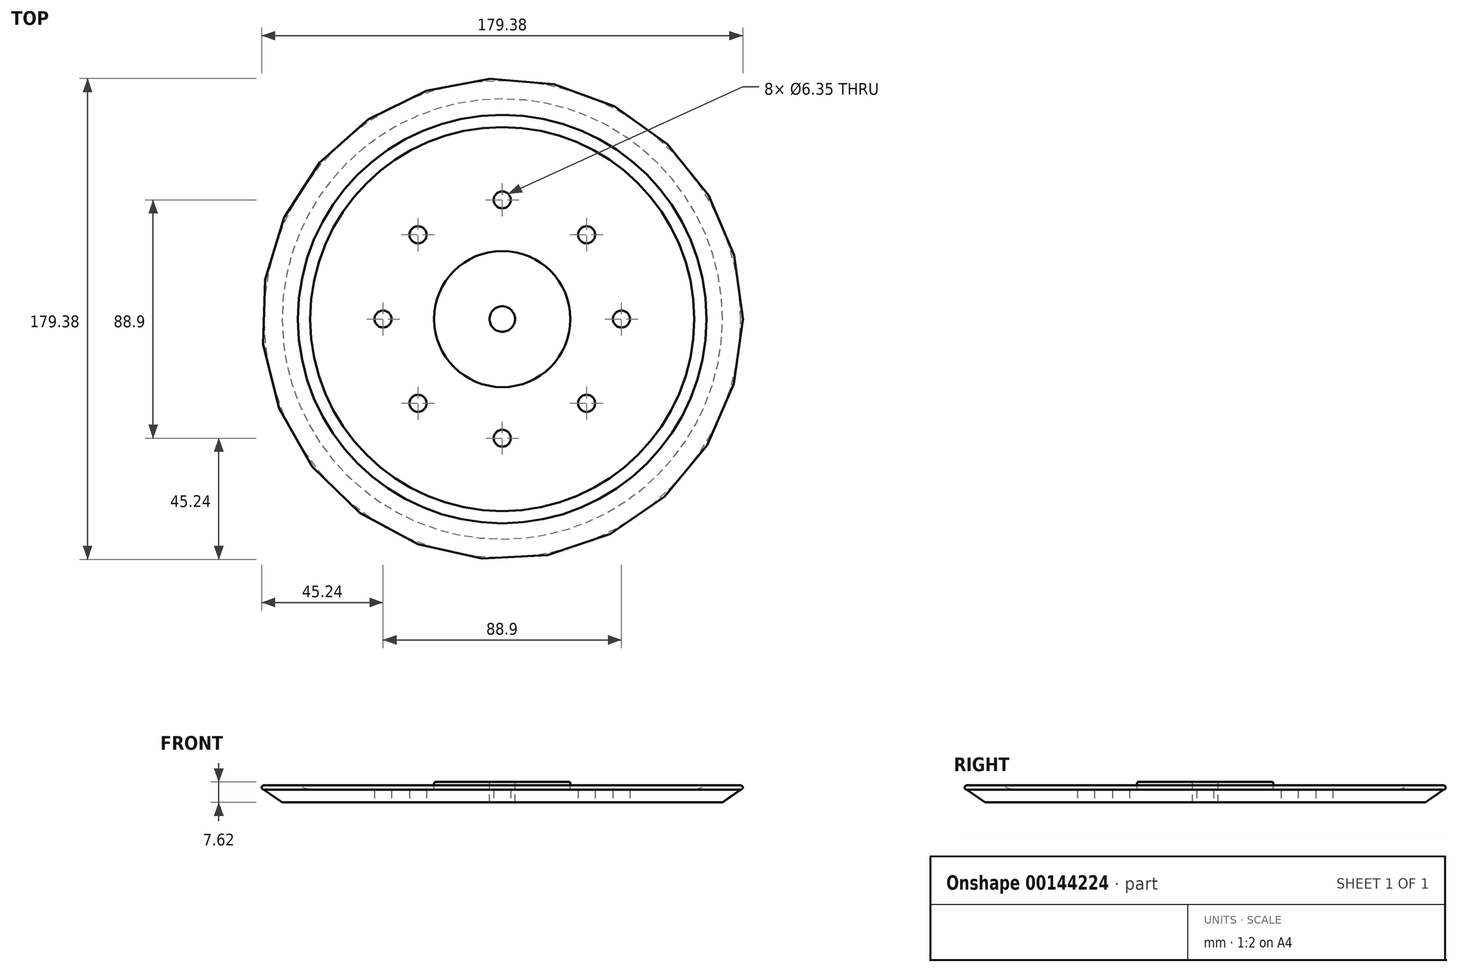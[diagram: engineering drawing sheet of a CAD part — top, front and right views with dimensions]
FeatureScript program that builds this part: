
annotation { "Feature Type Name" : "Feature", "Feature Type Description" : "" }
export const myFeature = defineFeature(function(context is Context, id is Id, definition is map)
    precondition{}
    {
        {
            var Q0;
            Q0=qCreatedBy(makeId("Front.planeOp"),FACE);
            var sketch = newSketch(context, id + "F0", { "sketchPlane" : qUnion([Q0])});
            skLineSegment(sketch, "E0", {"start": v(0, 0) * mm, "end": v(0, 7.62) * mm});
            skLineSegment(sketch, "E1", {"start": v(88.9, 4.76) * mm, "end": v(82.1, 0) * mm});
            skLineSegment(sketch, "E2", {"start": v(82.1, 0) * mm, "end": v(0, 0) * mm});
            skLineSegment(sketch, "E3", {"start": v(88.9, 6.35) * mm, "end": v(76.2, 6.35) * mm});
            skLineSegment(sketch, "E4", {"start": v(76.2, 6.35) * mm, "end": v(71.63, 4.57) * mm});
            skLineSegment(sketch, "E5", {"start": v(71.63, 4.57) * mm, "end": v(25.4, 4.57) * mm});
            skLineSegment(sketch, "E6", {"start": v(25.4, 4.57) * mm, "end": v(25.4, 7.1) * mm});
            skLineSegment(sketch, "E7", {"start": v(24.89, 7.62) * mm, "end": v(0, 7.62) * mm});
            skArc(sketch, "E8", {"start": v(88.9, 4.76) * mm, "mid": v(89.7, 5.56) * mm, "end": v(88.9, 6.35) * mm});
            skLineSegment(sketch, "E9.bottom", {"start": v(0, 7.62) * mm, "end": v(4.76, 7.62) * mm});
            skLineSegment(sketch, "E9.top", {"start": v(0, 0) * mm, "end": v(4.76, 0) * mm});
            skLineSegment(sketch, "E9.left", {"start": v(0, 7.62) * mm, "end": v(0, 0) * mm});
            skLineSegment(sketch, "E9.right", {"start": v(4.76, 7.62) * mm, "end": v(4.76, 0) * mm});
            skPoint(sketch, "E10.visualSharp", {"position": v(25.4, 7.62) * mm});
            skArc(sketch, "E10.filletArc", {"start": v(25.4, 7.1) * mm, "mid": v(25.25, 7.47) * mm, "end": v(24.89, 7.62) * mm});
            skSolve(sketch);
        }
        {
            var Q0;
            Q0=makeQuery(id+"F0.imprint","IMPRINT",FACE,{"disambiguationData":[TD([[makeQuery(id+"F0.imprint","IMPRINT",EDGE,{"derivedFrom":sQuery(id+"F0.wireOp",EDGE,"E1")}),-1.0]])]});
            var Q1;
            Q1=sQuery(id+"F0.wireOp",EDGE,"E9.left");
            revolve(context, id + "F1", {"entities" : qUnion([Q0]), "axis" : qUnion([Q1]), "revolveType" : RevolveType.FULL});
        }
        {
            var Q0;
            Q0=makeQuery(id+"F1.opRevolve","SWEPT_FACE",FACE,{"disambiguationData":[OSD([sQuery(id+"F0.wireOp",EDGE,"E5")])]});
            var sketch = newSketch(context, id + "F2", { "sketchPlane" : qUnion([Q0])});
            skPoint(sketch, "E11", {"position": v(0, 44.45) * mm});
            skPoint(sketch, "E12.1.0", {"position": v(-31.43, 31.43) * mm});
            skPoint(sketch, "E12.2.0", {"position": v(-44.45, 0) * mm});
            skPoint(sketch, "E12.center", {"position": v(0, 0) * mm});
            skPoint(sketch, "E13.0.3.0", {"position": v(-31.43, -31.43) * mm});
            skPoint(sketch, "E13.0.4.0", {"position": v(0, -44.45) * mm});
            skPoint(sketch, "E13.0.5.0", {"position": v(31.43, -31.43) * mm});
            skPoint(sketch, "E13.0.6.0", {"position": v(44.45, 0) * mm});
            skPoint(sketch, "E13.0.7.0", {"position": v(31.43, 31.43) * mm});
            skSolve(sketch);
        }
        {
            var Q0;
            Q0=sQuery(id+"F2.wireOp",VERTEX,"E11");
            var Q1;
            Q1=sQuery(id+"F2.wireOp",VERTEX,"E13.0.7.0");
            var Q2;
            Q2=sQuery(id+"F2.wireOp",VERTEX,"E13.0.6.0");
            var Q3;
            Q3=sQuery(id+"F2.wireOp",VERTEX,"E13.0.5.0");
            var Q4;
            Q4=sQuery(id+"F2.wireOp",VERTEX,"E13.0.4.0");
            var Q5;
            Q5=sQuery(id+"F2.wireOp",VERTEX,"E13.0.3.0");
            var Q6;
            Q6=sQuery(id+"F2.wireOp",VERTEX,"E12.2.0");
            var Q7;
            Q7=sQuery(id+"F2.wireOp",VERTEX,"E12.1.0");
            var Q8;
            Q8=makeQuery(id+"F1.opRevolve","SWEPT_BODY",BODY,{"disambiguationData":[OSD([sQuery(id+"F0.wireOp",EDGE,"E1"),sQuery(id+"F0.wireOp",EDGE,"E2"),sQuery(id+"F0.wireOp",EDGE,"E3"),sQuery(id+"F0.wireOp",EDGE,"E4"),sQuery(id+"F0.wireOp",EDGE,"E5"),sQuery(id+"F0.wireOp",EDGE,"E6"),sQuery(id+"F0.wireOp",EDGE,"E7"),sQuery(id+"F0.wireOp",EDGE,"E8"),sQuery(id+"F0.wireOp",EDGE,"E9.right"),sQuery(id+"F0.wireOp",EDGE,"E10.filletArc")])]});
            hole(context, id + "F3", {"style" : HoleStyle.SIMPLE, "endStyle" : HoleEndStyle.THROUGH, "holeDiameter" : 6.35 * mm, "locations" : qUnion([Q0, Q1, Q2, Q3, Q4, Q5, Q6, Q7]), "scope" : qUnion([Q8]), "isTappedThrough" : true});
        }
    });
